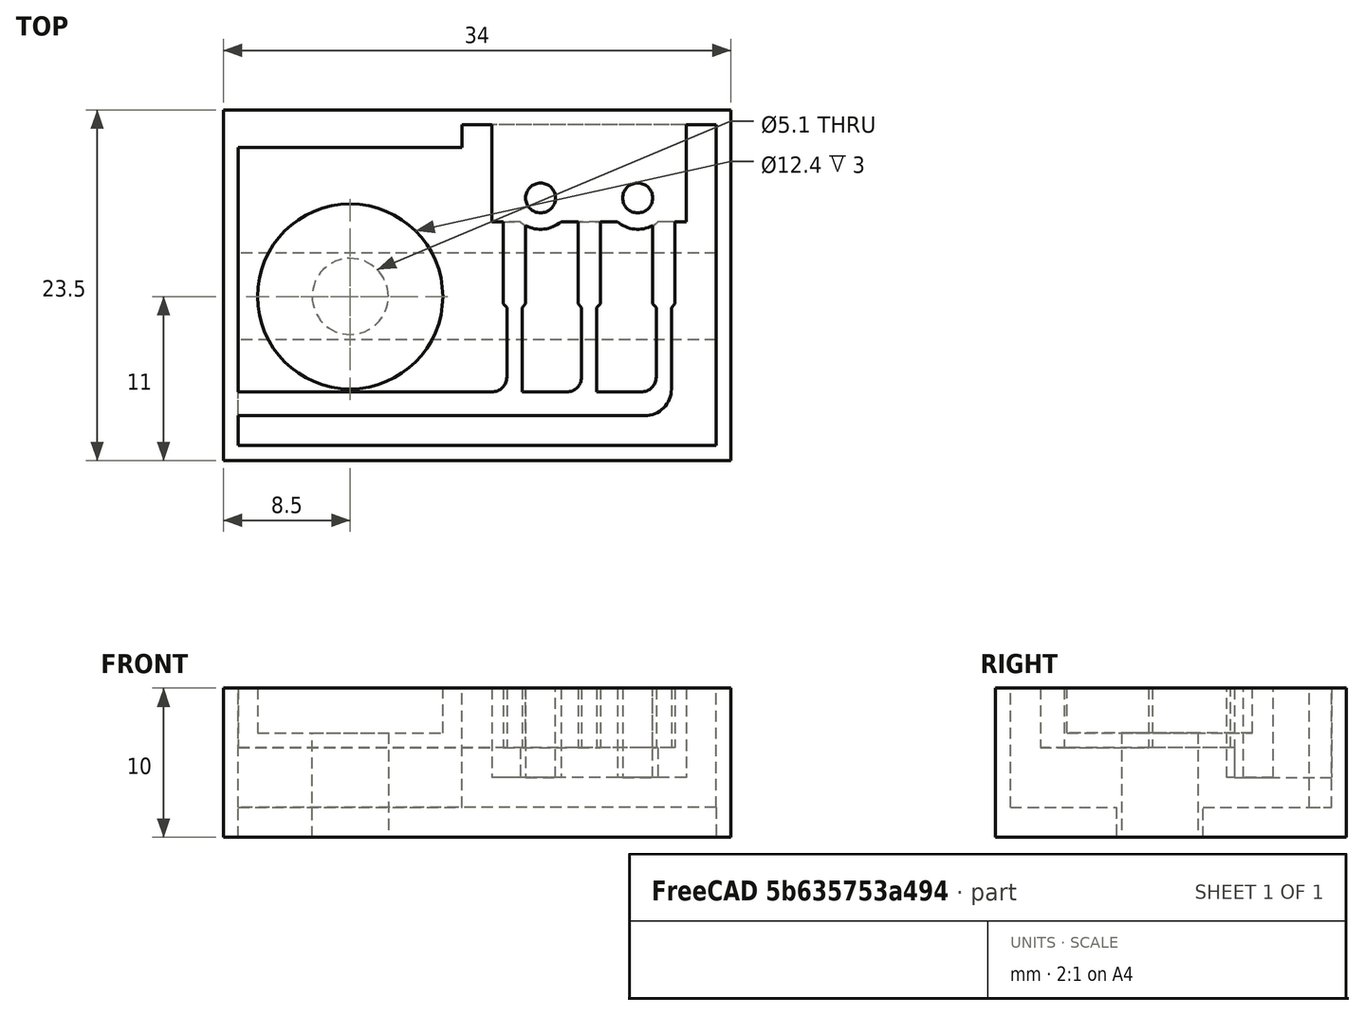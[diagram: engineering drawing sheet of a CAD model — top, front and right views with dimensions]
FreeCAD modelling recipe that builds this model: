
FCSTD DOCUMENT  (FreeCAD 0.18R16131 (Git))
Label: Limit Switch Bed - TopMirror  Job
License: All rights reserved
LicenseURL: http://es.wikipedia.org/wiki/Todos_los_derechos_reservados
objects: Path::FeaturePython×20, Part::FeaturePython×4, App::FeaturePython×2, App::DocumentObjectGroup×2, Mesh::FeaturePython×2, Path::FeatureCompoundPython×2, Part::Feature×1, Part::Mirroring×1
note: 11 computed .brp shape members not serialized (recipe doc carries the construction recipe); baked Part::Feature solids carry a one-line shape summary decoded from their .brp

FEATURE [App::FeaturePython] SetupSheet  # Path/CAM operation (typed FeaturePython)
  ClearanceHeightExpression = OpStockZMax+SetupSheet.ClearanceHeightOffset
  ClearanceHeightOffset = 5
  FinalDepthExpression = OpFinalDepth
  HorizRapid = 0
  SafeHeightExpression = OpStockZMax+SetupSheet.SafeHeightOffset
  SafeHeightOffset = 3
  StartDepthExpression = OpStartDepth
  StepDownExpression = OpToolDiameter
  VertRapid = 0
FEATURE [Path::FeaturePython] T3__SingleFlute2mm  label="T3: SingleFlute2mm"  # Path/CAM operation (typed FeaturePython)
  HorizFeed = 25
  HorizRapid = 0
  SpindleDir = 0
  SpindleSpeed = 8000
  ToolNumber = 3
  VertFeed = 5
  VertRapid = 0
  expr: HorizRapid = SetupSheet.HorizRapid
  expr: VertRapid = SetupSheet.VertRapid
FEATURE [Path::FeaturePython] T4__CornTeeth1mm  label="T4: SingleFlute1mm"  # Path/CAM operation (typed FeaturePython)
  HorizFeed = 25
  HorizRapid = 0
  SpindleDir = 0
  SpindleSpeed = 8000
  ToolNumber = 4
  VertFeed = 5
  VertRapid = 0
  expr: HorizRapid = SetupSheet.HorizRapid
  expr: VertRapid = SetupSheet.VertRapid
FEATURE [Path::FeaturePython] T5__Drill1mml  label="T5: Drill1mml"  # Path/CAM operation (typed FeaturePython)
  HorizFeed = 0
  HorizRapid = 0
  SpindleDir = 0
  SpindleSpeed = 0
  ToolNumber = 5
  VertFeed = 0
  VertRapid = 0
  expr: HorizRapid = SetupSheet.HorizRapid
  expr: VertRapid = SetupSheet.VertRapid
FEATURE [Path::FeaturePython] T6__Drill2mm  label="T6: Drill2mm"  # Path/CAM operation (typed FeaturePython)
  HorizFeed = 0
  HorizRapid = 0
  SpindleDir = 0
  SpindleSpeed = 0
  ToolNumber = 6
  VertFeed = 0
  VertRapid = 0
  expr: HorizRapid = SetupSheet.HorizRapid
  expr: VertRapid = SetupSheet.VertRapid
FEATURE [Part::Feature] Part__Feature  label="LimitSwitchBed"
  shape: bbox 32 x 21.5 x 10 mm, 57 faces (baked)
FEATURE [Part::Mirroring] mirror  label="Mirror of LimitSwitchBed"
  Base = (0,0,10)
  Normal = (1,0,0)
  Placement = pos=(32,0,0) rot=(0,0,1;0rad)
  Source = -> Part__Feature
FEATURE [Part::FeaturePython] Clone  label="Model-Body"  # Draft clone (typed FeaturePython)
  AttacherType = Attacher::AttachEngine3D
  Fuse = false
  Objects = -> [mirror]
  PathResource = Model
  Placement = pos=(32,0,0) rot=(0,0,1;0rad)
  Scale = (1,1,1)
FEATURE [App::DocumentObjectGroup] Model
  Group = -> [Clone]
FEATURE [Part::FeaturePython] Stock  # WARN: FeaturePython — macro-defined, semantics opaque (R4)
  Base = -> Model
  ExtXneg = 1
  ExtXpos = 1
  ExtYneg = 1
  ExtYpos = 1
  ExtZneg = 0
  ExtZpos = 0
  StockType = FromBase
FEATURE [Mesh::FeaturePython] CutMaterial  # WARN: FeaturePython — macro-defined, semantics opaque (R4)
FEATURE [Path::FeaturePython] Profile_Faces  # Path/CAM operation (typed FeaturePython)
  Active = true
  AreaParams:
    Tolerance = 1e-07
    FitArcs = True
    Simplify = False
    CleanDistance = 0.0
    Accuracy = 0.01
    Unit = 1.0
    MinArcPoints = 4
    MaxArcPoints = 100
    ClipperScale = 10000000.0
    Fill = 0
    Coplanar = 0
    Reorient = True
    Outline = False
    Explode = False
    OpenMode = 0
    Deflection = 0.01
    SubjectFill = 0
    ClipFill = 0
    Offset = -0.5
    ExtraPass = 0
    Stepover = 0.0
    LastStepover = 0.0
    JoinType = 0
    EndType = 0
    MiterLimit = 2.0
    RoundPrecision = 0.0
    PocketMode = 0
    ToolRadius = 1.0
    PocketExtraOffset = 0.0
    PocketStepover = 0.0
    PocketLastStepover = 0.0
    FromCenter = False
    Angle = 45.0
    AngleShift = 0.0
    Shift = 0.0
    Thicken = False
    SectionCount = -1
    Stepdown = 1.0
    SectionOffset = 0.0
    SectionTolerance = 1e-06
    SectionMode = 2
    Project = False
  Base = -> [Clone]
  ClearanceHeight = 15
  Direction = 0
  FinalDepth = 6
  JoinType = 0
  MiterLimit = 0.1
  OffsetExtra = 0
  OpFinalDepth = 6
  OpStartDepth = 10
  OpStockZMax = 10
  OpStockZMin = 0
  OpToolDiameter = 1
  PathParams = {'orientation': 1, 'feedrate': 25.0, 'feedrate_v': 5.0, 'verbose': True, 'resume_height': 13.0, 'retraction': 15.0, 'return_end': True, 'preamble': False}
  SafeHeight = 13
  Side = 1
  StartDepth = 10
  StartPoint = (0,0,0)
  StepDown = 0.2
  ToolController = -> T4__CornTeeth1mm
  UseComp = true
  UseStartPoint = false
  processCircles = false
  processHoles = false
  processPerimeter = true
  expr: ClearanceHeight = OpStockZMax + SetupSheet.ClearanceHeightOffset
  expr: SafeHeight = OpStockZMax + SetupSheet.SafeHeightOffset
  expr: StepDown = OpToolDiameter / 5
  expr: FinalDepth = OpFinalDepth
  expr: StartDepth = OpStartDepth
FEATURE [Path::FeaturePython] DogboneDressup  label="CableGuide"  # Path/CAM operation (typed FeaturePython)
  Base = -> Profile_Faces
  BoneBlacklist = [1,2,4,9,11,12,14,19,21,22,24,29,31,32,34,39,41,42,44,49,51,52,54,59,61,62,64,69,71,72,74,79,81,82,84,89,91,92,94,99,101,102,104,109,111,112,114,119,121,122,124,129,131,132,134,139,141,142,144,149,151,+19 more]
  Custom = 0
  Incision = 1
  Side = 0
  Style = 2
FEATURE [Path::FeaturePython] Pocket_Shape  label="_SwitchBed"  # Path/CAM operation (typed FeaturePython)
  Active = true
  AreaParams:
    Tolerance = 1e-07
    FitArcs = True
    Simplify = False
    CleanDistance = 0.0
    Accuracy = 0.01
    Unit = 1.0
    MinArcPoints = 4
    MaxArcPoints = 100
    ClipperScale = 10000000.0
    Fill = 0
    Coplanar = 0
    Reorient = True
    Outline = False
    Explode = False
    OpenMode = 0
    Deflection = 0.01
    SubjectFill = 0
    ClipFill = 0
    Offset = 0.0
    ExtraPass = 0
    Stepover = 0.0
    LastStepover = 0.0
    JoinType = 0
    EndType = 0
    MiterLimit = 2.0
    RoundPrecision = 0.0
    PocketMode = 2
    ToolRadius = 0.5
    PocketExtraOffset = 0.0
    PocketStepover = 0.6
    PocketLastStepover = 0.0
    FromCenter = True
    Angle = 45.0
    AngleShift = 0.0
    Shift = 0.0
    Thicken = False
    SectionCount = -1
    Stepdown = 1.0
    SectionOffset = 0.0
    SectionTolerance = 1e-06
    SectionMode = 2
    Project = False
  Base = -> [Clone]
  ClearanceHeight = 15
  CutMode = 0
  ExtraOffset = 0
  FinalDepth = 4
  FinishDepth = 0
  KeepToolDown = false
  MinTravel = false
  OffsetPattern = 1
  OpFinalDepth = 4
  OpStartDepth = 10
  OpStockZMax = 10
  OpStockZMin = 0
  OpToolDiameter = 1
  PathParams = {'orientation': 1, 'feedrate': 25.0, 'feedrate_v': 5.0, 'verbose': True, 'resume_height': 13.0, 'retraction': 15.0, 'return_end': True, 'preamble': False}
  SafeHeight = 13
  StartAt = 0
  StartDepth = 10
  StartPoint = (0,0,0)
  StepDown = 0.2
  StepOver = 60
  ToolController = -> T4__CornTeeth1mm
  UseOutline = false
  UseStartPoint = false
  ZigZagAngle = 45
  expr: ClearanceHeight = OpStockZMax + SetupSheet.ClearanceHeightOffset
  expr: SafeHeight = OpStockZMax + SetupSheet.SafeHeightOffset
  expr: StepDown = OpToolDiameter / 5
  expr: FinalDepth = OpFinalDepth
  expr: StartDepth = OpStartDepth
FEATURE [Path::FeaturePython] DogboneDressup001  label="SwitchBed"  # Path/CAM operation (typed FeaturePython)
  Base = -> Pocket_Shape
  BoneBlacklist = [5,6,7,8,9,10,11,12,13,14,15,16,17,18,27,28,29,30,31,32,33,34,35,36,37,38,39,40,49,50,51,52,53,54,55,56,57,58,59,60,61,62,71,72,73,74,75,76,77,78,79,80,81,82,83,84,93,94,95,96,97,98,99,100,101,102,103,+143 more]
  Custom = 0
  Incision = 0
  Side = 1
  Style = 0
FEATURE [Path::FeatureCompoundPython] Operations  # Path/CAM operation (typed FeaturePython)
  Group = -> [DogboneDressup,DogboneDressup001]
  UsePlacements = false
FEATURE [Path::FeaturePython] Job  label="Top-Job-1mm"  # Path/CAM operation (typed FeaturePython)
  GeometryTolerance = 0.01
  Model = -> Model
  Operations = -> Operations
  PostProcessor = 2
  PostProcessorOutputFile = <userpath>/prj/LimitSwitchBed/LSB-TopMirror-1mm.gcode
  SetupSheet = -> SetupSheet
  Stock = -> Stock
  ToolController = -> [T3__SingleFlute2mm,T4__CornTeeth1mm,T5__Drill1mml,T6__Drill2mm]
FEATURE [Part::FeaturePython] Clone001  label="Model-Body001"  # Draft clone (typed FeaturePython)
  AttacherType = Attacher::AttachEngine3D
  Fuse = false
  Objects = -> [mirror]
  PathResource = Model
  Placement = pos=(32,0,0) rot=(0,0,1;0rad)
  Scale = (1,1,1)
FEATURE [Path::FeaturePython] T3__SingleFlute2mm001  label="T3: SingleFlute2mm001"  # Path/CAM operation (typed FeaturePython)
  HorizFeed = 25
  HorizRapid = 0
  SpindleDir = 0
  SpindleSpeed = 8000
  ToolNumber = 3
  VertFeed = 5
  VertRapid = 0
  expr: HorizRapid = SetupSheet001.HorizRapid
  expr: VertRapid = SetupSheet001.VertRapid
FEATURE [Path::FeaturePython] T4__CornTeeth1mm001  label="T4: SingleFlute1mm001"  # Path/CAM operation (typed FeaturePython)
  HorizFeed = 25
  HorizRapid = 0
  SpindleDir = 0
  SpindleSpeed = 8000
  ToolNumber = 4
  VertFeed = 5
  VertRapid = 0
  expr: HorizRapid = SetupSheet001.HorizRapid
  expr: VertRapid = SetupSheet001.VertRapid
FEATURE [Path::FeaturePython] T5__Drill1mml001  label="T5: Drill1mml001"  # Path/CAM operation (typed FeaturePython)
  HorizFeed = 0
  HorizRapid = 0
  SpindleDir = 0
  SpindleSpeed = 0
  ToolNumber = 5
  VertFeed = 0
  VertRapid = 0
  expr: HorizRapid = SetupSheet001.HorizRapid
  expr: VertRapid = SetupSheet001.VertRapid
FEATURE [Path::FeaturePython] T6__Drill2mm001  label="T6: Drill2mm001"  # Path/CAM operation (typed FeaturePython)
  HorizFeed = 0
  HorizRapid = 0
  SpindleDir = 0
  SpindleSpeed = 0
  ToolNumber = 6
  VertFeed = 0
  VertRapid = 0
  expr: HorizRapid = SetupSheet001.HorizRapid
  expr: VertRapid = SetupSheet001.VertRapid
FEATURE [App::FeaturePython] SetupSheet001  # Path/CAM operation (typed FeaturePython)
  ClearanceHeightExpression = OpStockZMax+SetupSheet.ClearanceHeightOffset
  ClearanceHeightOffset = 5
  FinalDepthExpression = OpFinalDepth
  HorizRapid = 0
  SafeHeightExpression = OpStockZMax+SetupSheet.SafeHeightOffset
  SafeHeightOffset = 3
  StartDepthExpression = OpStartDepth
  StepDownExpression = OpToolDiameter
  VertRapid = 0
FEATURE [App::DocumentObjectGroup] Model001
  Group = -> [Clone001]
FEATURE [Part::FeaturePython] Stock001  # WARN: FeaturePython — macro-defined, semantics opaque (R4)
  Base = -> Model001
  ExtXneg = 1
  ExtXpos = 1
  ExtYneg = 1
  ExtYpos = 1
  ExtZneg = 0
  ExtZpos = 0
  StockType = FromBase
FEATURE [Path::FeaturePython] Contour006  label="Exterior Contour"  # Path/CAM operation (typed FeaturePython)
  Active = true
  AreaParams:
    Tolerance = 1e-07
    FitArcs = True
    Simplify = False
    CleanDistance = 0.0
    Accuracy = 0.01
    Unit = 1.0
    MinArcPoints = 4
    MaxArcPoints = 100
    ClipperScale = 10000000.0
    Fill = 0
    Coplanar = 2
    Reorient = True
    Outline = False
    Explode = False
    OpenMode = 0
    Deflection = 0.01
    SubjectFill = 0
    ClipFill = 0
    Offset = 2.0
    ExtraPass = 0
    Stepover = 0.0
    LastStepover = 0.0
    JoinType = 0
    EndType = 0
    MiterLimit = 2.0
    RoundPrecision = 0.0
    PocketMode = 0
    ToolRadius = 1.0
    PocketExtraOffset = 0.0
    PocketStepover = 0.0
    PocketLastStepover = 0.0
    FromCenter = False
    Angle = 45.0
    AngleShift = 0.0
    Shift = 0.0
    Thicken = False
    SectionCount = -1
    Stepdown = 1.0
    SectionOffset = 0.0
    SectionTolerance = 1e-06
    SectionMode = 2
    Project = False
  ClearanceHeight = 15
  Direction = 0
  FinalDepth = 3
  JoinType = 0
  MiterLimit = 0.1
  OffsetExtra = 1
  OpFinalDepth = 0
  OpStartDepth = 10
  OpStockZMax = 10
  OpStockZMin = 0
  OpToolDiameter = 2
  PathParams = {'orientation': 1, 'feedrate': 25.0, 'feedrate_v': 5.0, 'verbose': True, 'resume_height': 13.0, 'retraction': 15.0, 'return_end': True, 'preamble': False}
  SafeHeight = 13
  Side = 0
  StartDepth = 10
  StartPoint = (0,0,0)
  StepDown = 2
  ToolController = -> T3__SingleFlute2mm001
  UseComp = true
  UseStartPoint = false
  expr: ClearanceHeight = OpStockZMax + SetupSheet.ClearanceHeightOffset
  expr: SafeHeight = OpStockZMax + SetupSheet.SafeHeightOffset
  expr: StepDown = OpToolDiameter
  expr: FinalDepth = 3
  expr: StartDepth = OpStartDepth
FEATURE [Path::FeaturePython] Contour007  label="_Bottom Contour"  # Path/CAM operation (typed FeaturePython)
  Active = true
  AreaParams:
    Tolerance = 1e-07
    FitArcs = True
    Simplify = False
    CleanDistance = 0.0
    Accuracy = 0.01
    Unit = 1.0
    MinArcPoints = 4
    MaxArcPoints = 100
    ClipperScale = 10000000.0
    Fill = 0
    Coplanar = 2
    Reorient = True
    Outline = False
    Explode = False
    OpenMode = 0
    Deflection = 0.01
    SubjectFill = 0
    ClipFill = 0
    Offset = 1.5
    ExtraPass = 0
    Stepover = 0.0
    LastStepover = 0.0
    JoinType = 0
    EndType = 0
    MiterLimit = 2.0
    RoundPrecision = 0.0
    PocketMode = 0
    ToolRadius = 1.0
    PocketExtraOffset = 0.0
    PocketStepover = 0.0
    PocketLastStepover = 0.0
    FromCenter = False
    Angle = 45.0
    AngleShift = 0.0
    Shift = 0.0
    Thicken = False
    SectionCount = -1
    Stepdown = 1.0
    SectionOffset = 0.0
    SectionTolerance = 1e-06
    SectionMode = 2
    Project = False
  ClearanceHeight = 15
  Direction = 0
  FinalDepth = 0
  JoinType = 0
  MiterLimit = 0.1
  OffsetExtra = 0.5
  OpFinalDepth = 0
  OpStartDepth = 10
  OpStockZMax = 10
  OpStockZMin = 0
  OpToolDiameter = 2
  PathParams = {'orientation': 1, 'feedrate': 25.0, 'feedrate_v': 5.0, 'verbose': True, 'resume_height': 13.0, 'retraction': 15.0, 'return_end': True, 'preamble': False}
  SafeHeight = 13
  Side = 0
  StartDepth = 3
  StartPoint = (0,0,0)
  StepDown = 2
  ToolController = -> T3__SingleFlute2mm001
  UseComp = true
  UseStartPoint = false
  expr: ClearanceHeight = OpStockZMax + SetupSheet.ClearanceHeightOffset
  expr: SafeHeight = OpStockZMax + SetupSheet.SafeHeightOffset
  expr: StepDown = OpToolDiameter
  expr: FinalDepth = OpFinalDepth
  expr: StartDepth = 3
FEATURE [Path::FeaturePython] Helix002  label="WashBed"  # Path/CAM operation (typed FeaturePython)
  Active = true
  Base = -> [Clone001]
  ClearanceHeight = 15
  Direction = 0
  FinalDepth = 7.5
  OpFinalDepth = 10
  OpStartDepth = 12
  OpStockZMax = 10
  OpStockZMin = 0
  OpToolDiameter = 2
  SafeHeight = 13
  StartDepth = 10
  StartSide = 0
  StepDown = 2
  StepOver = 90
  ToolController = -> T3__SingleFlute2mm001
  expr: ClearanceHeight = OpStockZMax + SetupSheet.ClearanceHeightOffset
  expr: SafeHeight = OpStockZMax + SetupSheet.SafeHeightOffset
  expr: StepDown = OpToolDiameter
  expr: FinalDepth = 7.5
  expr: StartDepth = 10
FEATURE [Path::FeaturePython] Helix003  label="BoltHole"  # Path/CAM operation (typed FeaturePython)
  Active = true
  Base = -> [Clone001]
  ClearanceHeight = 15
  Direction = 0
  FinalDepth = 0
  OpFinalDepth = 7
  OpStartDepth = 10
  OpStockZMax = 10
  OpStockZMin = 0
  OpToolDiameter = 2
  SafeHeight = 13
  StartDepth = 7
  StartSide = 0
  StepDown = 2
  StepOver = 100
  ToolController = -> T3__SingleFlute2mm001
  expr: ClearanceHeight = OpStockZMax + SetupSheet.ClearanceHeightOffset
  expr: SafeHeight = OpStockZMax + SetupSheet.SafeHeightOffset
  expr: StepDown = OpToolDiameter
  expr: FinalDepth = 0
  expr: StartDepth = OpFinalDepth
FEATURE [Path::FeaturePython] Contour008  label="Interior Contour"  # Path/CAM operation (typed FeaturePython)
  Active = true
  AreaParams:
    Tolerance = 1e-07
    FitArcs = True
    Simplify = False
    CleanDistance = 0.0
    Accuracy = 0.01
    Unit = 1.0
    MinArcPoints = 4
    MaxArcPoints = 100
    ClipperScale = 10000000.0
    Fill = 0
    Coplanar = 2
    Reorient = True
    Outline = False
    Explode = False
    OpenMode = 0
    Deflection = 0.01
    SubjectFill = 0
    ClipFill = 0
    Offset = 1.0
    ExtraPass = 0
    Stepover = 0.0
    LastStepover = 0.0
    JoinType = 0
    EndType = 0
    MiterLimit = 2.0
    RoundPrecision = 0.0
    PocketMode = 0
    ToolRadius = 1.0
    PocketExtraOffset = 0.0
    PocketStepover = 0.0
    PocketLastStepover = 0.0
    FromCenter = False
    Angle = 45.0
    AngleShift = 0.0
    Shift = 0.0
    Thicken = False
    SectionCount = -1
    Stepdown = 1.0
    SectionOffset = 0.0
    SectionTolerance = 1e-06
    SectionMode = 2
    Project = False
  ClearanceHeight = 15
  Direction = 0
  FinalDepth = 3
  JoinType = 0
  MiterLimit = 0.1
  OffsetExtra = 0
  OpFinalDepth = 0
  OpStartDepth = 10
  OpStockZMax = 10
  OpStockZMin = 0
  OpToolDiameter = 2
  PathParams = {'orientation': 1, 'feedrate': 25.0, 'feedrate_v': 5.0, 'verbose': True, 'resume_height': 13.0, 'retraction': 15.0, 'return_end': True, 'preamble': False}
  SafeHeight = 13
  Side = 0
  StartDepth = 10
  StartPoint = (0,0,0)
  StepDown = 2
  ToolController = -> T3__SingleFlute2mm001
  UseComp = true
  UseStartPoint = false
  expr: ClearanceHeight = OpStockZMax + SetupSheet.ClearanceHeightOffset
  expr: SafeHeight = OpStockZMax + SetupSheet.SafeHeightOffset
  expr: StepDown = OpToolDiameter
  expr: FinalDepth = 3
  expr: StartDepth = OpStartDepth
FEATURE [Path::FeaturePython] TagDressup  # Path/CAM operation (typed FeaturePython)
  Angle = 45
  Base = -> Contour007
  Disabled = [2]
  Height = 0.5
  Positions = (5) [(33.5,10.75,0),(16,-1.5,0),(8,-1.5,0),(-1.5,10,0),(23.5,23,0)]
  Radius = 0
  SegmentationFactor = 50
  Width = 2
FEATURE [Path::FeatureCompoundPython] Operations001  # Path/CAM operation (typed FeaturePython)
  Group = -> [Helix002,Helix003,Contour008,Contour006,TagDressup]
  UsePlacements = false
FEATURE [Path::FeaturePython] Job001  label="Top-Job-2mm"  # Path/CAM operation (typed FeaturePython)
  GeometryTolerance = 0.01
  Model = -> Model001
  Operations = -> Operations001
  PostProcessor = 2
  PostProcessorOutputFile = <userpath>/prj/LimitSwitchBed/LSB-TopMirror-2mm.gcode
  SetupSheet = -> SetupSheet001
  Stock = -> Stock001
  ToolController = -> [T3__SingleFlute2mm001,T4__CornTeeth1mm001,T5__Drill1mml001,T6__Drill2mm001]
FEATURE [Mesh::FeaturePython] CutMaterial001  # WARN: FeaturePython — macro-defined, semantics opaque (R4)
